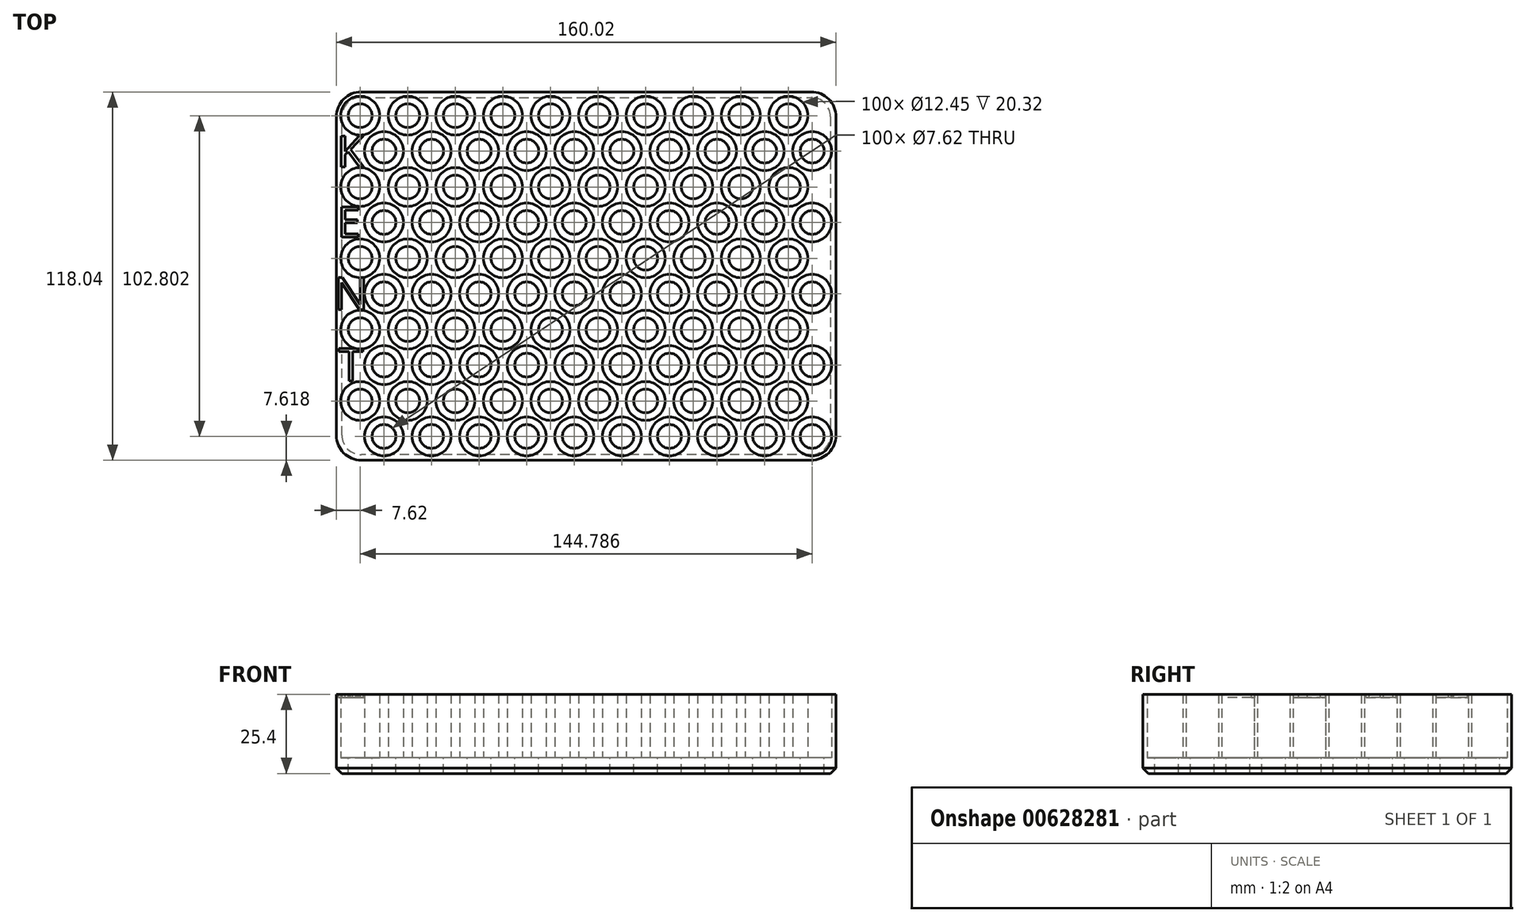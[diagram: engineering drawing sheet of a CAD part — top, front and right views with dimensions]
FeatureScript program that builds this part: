
annotation { "Feature Type Name" : "Feature", "Feature Type Description" : "" }
export const myFeature = defineFeature(function(context is Context, id is Id, definition is map)
    precondition{}
    {
        {
            var Q0;
            Q0=qCreatedBy(makeId("Top.planeOp"),FACE);
            var sketch = newSketch(context, id + "F0", { "sketchPlane" : qUnion([Q0])});
            skLineSegment(sketch, "E0.bottom", {"start": v(76.2, 76.2) * mm, "end": v(-76.2, 76.2) * mm});
            skLineSegment(sketch, "E0.right", {"start": v(-76.2, 76.2) * mm, "end": v(-76.2, -41.84) * mm});
            skPoint(sketch, "E0.middle", {"position": v(0, 0) * mm});
            skCircle(sketch, "E1", {"center": v(-68.58, 68.58) * mm, "radius": 6.22 * mm});
            skCircle(sketch, "E2", {"center": v(-68.58, 68.58) * mm, "radius": 3.81 * mm});
            skCircle(sketch, "E3.1.0.0", {"center": v(-53.34, 68.58) * mm, "radius": 3.81 * mm});
            skCircle(sketch, "E3.1.0.1", {"center": v(-53.34, 68.58) * mm, "radius": 6.22 * mm});
            skCircle(sketch, "E3.2.0.0", {"center": v(-38.1, 68.58) * mm, "radius": 3.81 * mm});
            skCircle(sketch, "E3.2.0.1", {"center": v(-38.1, 68.58) * mm, "radius": 6.22 * mm});
            skCircle(sketch, "E3.3.0.0", {"center": v(-22.86, 68.58) * mm, "radius": 3.81 * mm});
            skCircle(sketch, "E3.3.0.1", {"center": v(-22.86, 68.58) * mm, "radius": 6.22 * mm});
            skCircle(sketch, "E3.4.0.0", {"center": v(-7.62, 68.58) * mm, "radius": 3.81 * mm});
            skCircle(sketch, "E3.4.0.1", {"center": v(-7.62, 68.58) * mm, "radius": 6.22 * mm});
            skCircle(sketch, "E3.5.0.0", {"center": v(7.62, 68.58) * mm, "radius": 3.81 * mm});
            skCircle(sketch, "E3.5.0.1", {"center": v(7.62, 68.58) * mm, "radius": 6.22 * mm});
            skCircle(sketch, "E3.6.0.0", {"center": v(22.86, 68.58) * mm, "radius": 3.81 * mm});
            skCircle(sketch, "E3.6.0.1", {"center": v(22.86, 68.58) * mm, "radius": 6.22 * mm});
            skCircle(sketch, "E3.7.0.0", {"center": v(38.1, 68.58) * mm, "radius": 3.81 * mm});
            skCircle(sketch, "E3.7.0.1", {"center": v(38.1, 68.58) * mm, "radius": 6.22 * mm});
            skCircle(sketch, "E3.8.0.0", {"center": v(53.34, 68.58) * mm, "radius": 3.81 * mm});
            skCircle(sketch, "E3.8.0.1", {"center": v(53.34, 68.58) * mm, "radius": 6.22 * mm});
            skCircle(sketch, "E3.9.0.0", {"center": v(68.58, 68.58) * mm, "radius": 3.81 * mm});
            skCircle(sketch, "E3.9.0.1", {"center": v(68.58, 68.58) * mm, "radius": 6.22 * mm});
            skCircle(sketch, "E4.1.0.0", {"center": v(-68.58, 45.72) * mm, "radius": 3.81 * mm});
            skCircle(sketch, "E4.1.0.1", {"center": v(-68.58, 45.72) * mm, "radius": 6.22 * mm});
            skCircle(sketch, "E4.1.0.2", {"center": v(-22.86, 45.72) * mm, "radius": 3.81 * mm});
            skCircle(sketch, "E4.1.0.3", {"center": v(-53.34, 45.72) * mm, "radius": 3.81 * mm});
            skCircle(sketch, "E4.1.0.4", {"center": v(-38.1, 45.72) * mm, "radius": 3.81 * mm});
            skCircle(sketch, "E4.1.0.5", {"center": v(-38.1, 45.72) * mm, "radius": 6.22 * mm});
            skCircle(sketch, "E4.1.0.6", {"center": v(7.62, 45.72) * mm, "radius": 6.22 * mm});
            skCircle(sketch, "E4.1.0.7", {"center": v(22.86, 45.72) * mm, "radius": 3.81 * mm});
            skCircle(sketch, "E4.1.0.8", {"center": v(-22.86, 45.72) * mm, "radius": 6.22 * mm});
            skCircle(sketch, "E4.1.0.9", {"center": v(38.1, 45.72) * mm, "radius": 6.22 * mm});
            skCircle(sketch, "E4.1.0.10", {"center": v(-53.34, 45.72) * mm, "radius": 6.22 * mm});
            skCircle(sketch, "E4.1.0.11", {"center": v(-7.62, 45.72) * mm, "radius": 3.81 * mm});
            skCircle(sketch, "E4.1.0.12", {"center": v(22.86, 45.72) * mm, "radius": 6.22 * mm});
            skCircle(sketch, "E4.1.0.13", {"center": v(-7.62, 45.72) * mm, "radius": 6.22 * mm});
            skCircle(sketch, "E4.1.0.14", {"center": v(38.1, 45.72) * mm, "radius": 3.81 * mm});
            skCircle(sketch, "E4.1.0.15", {"center": v(7.62, 45.72) * mm, "radius": 3.81 * mm});
            skCircle(sketch, "E4.1.0.16", {"center": v(68.58, 45.72) * mm, "radius": 3.81 * mm});
            skCircle(sketch, "E4.1.0.17", {"center": v(53.34, 45.72) * mm, "radius": 3.81 * mm});
            skCircle(sketch, "E4.1.0.18", {"center": v(68.58, 45.72) * mm, "radius": 6.22 * mm});
            skCircle(sketch, "E4.1.0.19", {"center": v(53.34, 45.72) * mm, "radius": 6.22 * mm});
            skCircle(sketch, "E4.2.0.0", {"center": v(-68.58, 22.86) * mm, "radius": 3.81 * mm});
            skCircle(sketch, "E4.2.0.1", {"center": v(-68.58, 22.86) * mm, "radius": 6.22 * mm});
            skCircle(sketch, "E4.2.0.2", {"center": v(-22.86, 22.86) * mm, "radius": 3.81 * mm});
            skCircle(sketch, "E4.2.0.3", {"center": v(-53.34, 22.86) * mm, "radius": 3.81 * mm});
            skCircle(sketch, "E4.2.0.4", {"center": v(-38.1, 22.86) * mm, "radius": 3.81 * mm});
            skCircle(sketch, "E4.2.0.5", {"center": v(-38.1, 22.86) * mm, "radius": 6.22 * mm});
            skCircle(sketch, "E4.2.0.6", {"center": v(7.62, 22.86) * mm, "radius": 6.22 * mm});
            skCircle(sketch, "E4.2.0.7", {"center": v(22.86, 22.86) * mm, "radius": 3.81 * mm});
            skCircle(sketch, "E4.2.0.8", {"center": v(-22.86, 22.86) * mm, "radius": 6.22 * mm});
            skCircle(sketch, "E4.2.0.9", {"center": v(38.1, 22.86) * mm, "radius": 6.22 * mm});
            skCircle(sketch, "E4.2.0.10", {"center": v(-53.34, 22.86) * mm, "radius": 6.22 * mm});
            skCircle(sketch, "E4.2.0.11", {"center": v(-7.62, 22.86) * mm, "radius": 3.81 * mm});
            skCircle(sketch, "E4.2.0.12", {"center": v(22.86, 22.86) * mm, "radius": 6.22 * mm});
            skCircle(sketch, "E4.2.0.13", {"center": v(-7.62, 22.86) * mm, "radius": 6.22 * mm});
            skCircle(sketch, "E4.2.0.14", {"center": v(38.1, 22.86) * mm, "radius": 3.81 * mm});
            skCircle(sketch, "E4.2.0.15", {"center": v(7.62, 22.86) * mm, "radius": 3.81 * mm});
            skCircle(sketch, "E4.2.0.16", {"center": v(68.58, 22.86) * mm, "radius": 3.81 * mm});
            skCircle(sketch, "E4.2.0.17", {"center": v(53.34, 22.86) * mm, "radius": 3.81 * mm});
            skCircle(sketch, "E4.2.0.18", {"center": v(68.58, 22.86) * mm, "radius": 6.22 * mm});
            skCircle(sketch, "E4.2.0.19", {"center": v(53.34, 22.86) * mm, "radius": 6.22 * mm});
            skCircle(sketch, "E4.3.0.0", {"center": v(-68.58, 0) * mm, "radius": 3.81 * mm});
            skCircle(sketch, "E4.3.0.1", {"center": v(-68.58, 0) * mm, "radius": 6.22 * mm});
            skCircle(sketch, "E4.3.0.2", {"center": v(-22.86, 0) * mm, "radius": 3.81 * mm});
            skCircle(sketch, "E4.3.0.3", {"center": v(-53.34, 0) * mm, "radius": 3.81 * mm});
            skCircle(sketch, "E4.3.0.4", {"center": v(-38.1, 0) * mm, "radius": 3.81 * mm});
            skCircle(sketch, "E4.3.0.5", {"center": v(-38.1, 0) * mm, "radius": 6.22 * mm});
            skCircle(sketch, "E4.3.0.6", {"center": v(7.62, 0) * mm, "radius": 6.22 * mm});
            skCircle(sketch, "E4.3.0.7", {"center": v(22.86, 0) * mm, "radius": 3.81 * mm});
            skCircle(sketch, "E4.3.0.8", {"center": v(-22.86, 0) * mm, "radius": 6.22 * mm});
            skCircle(sketch, "E4.3.0.9", {"center": v(38.1, 0) * mm, "radius": 6.22 * mm});
            skCircle(sketch, "E4.3.0.10", {"center": v(-53.34, 0) * mm, "radius": 6.22 * mm});
            skCircle(sketch, "E4.3.0.11", {"center": v(-7.62, 0) * mm, "radius": 3.81 * mm});
            skCircle(sketch, "E4.3.0.12", {"center": v(22.86, 0) * mm, "radius": 6.22 * mm});
            skCircle(sketch, "E4.3.0.13", {"center": v(-7.62, 0) * mm, "radius": 6.22 * mm});
            skCircle(sketch, "E4.3.0.14", {"center": v(38.1, 0) * mm, "radius": 3.81 * mm});
            skCircle(sketch, "E4.3.0.15", {"center": v(7.62, 0) * mm, "radius": 3.81 * mm});
            skCircle(sketch, "E4.3.0.16", {"center": v(68.58, 0) * mm, "radius": 3.81 * mm});
            skCircle(sketch, "E4.3.0.17", {"center": v(53.34, 0) * mm, "radius": 3.81 * mm});
            skCircle(sketch, "E4.3.0.18", {"center": v(68.58, 0) * mm, "radius": 6.22 * mm});
            skCircle(sketch, "E4.3.0.19", {"center": v(53.34, 0) * mm, "radius": 6.22 * mm});
            skCircle(sketch, "E4.4.0.0", {"center": v(-68.58, -22.86) * mm, "radius": 3.81 * mm});
            skCircle(sketch, "E4.4.0.1", {"center": v(-68.58, -22.86) * mm, "radius": 6.22 * mm});
            skCircle(sketch, "E4.4.0.2", {"center": v(-22.86, -22.86) * mm, "radius": 3.81 * mm});
            skCircle(sketch, "E4.4.0.3", {"center": v(-53.34, -22.86) * mm, "radius": 3.81 * mm});
            skCircle(sketch, "E4.4.0.4", {"center": v(-38.1, -22.86) * mm, "radius": 3.81 * mm});
            skCircle(sketch, "E4.4.0.5", {"center": v(-38.1, -22.86) * mm, "radius": 6.22 * mm});
            skCircle(sketch, "E4.4.0.6", {"center": v(7.62, -22.86) * mm, "radius": 6.22 * mm});
            skCircle(sketch, "E4.4.0.7", {"center": v(22.86, -22.86) * mm, "radius": 3.81 * mm});
            skCircle(sketch, "E4.4.0.8", {"center": v(-22.86, -22.86) * mm, "radius": 6.22 * mm});
            skCircle(sketch, "E4.4.0.9", {"center": v(38.1, -22.86) * mm, "radius": 6.22 * mm});
            skCircle(sketch, "E4.4.0.10", {"center": v(-53.34, -22.86) * mm, "radius": 6.22 * mm});
            skCircle(sketch, "E4.4.0.11", {"center": v(-7.62, -22.86) * mm, "radius": 3.81 * mm});
            skCircle(sketch, "E4.4.0.12", {"center": v(22.86, -22.86) * mm, "radius": 6.22 * mm});
            skCircle(sketch, "E4.4.0.13", {"center": v(-7.62, -22.86) * mm, "radius": 6.22 * mm});
            skCircle(sketch, "E4.4.0.14", {"center": v(38.1, -22.86) * mm, "radius": 3.81 * mm});
            skCircle(sketch, "E4.4.0.15", {"center": v(7.62, -22.86) * mm, "radius": 3.81 * mm});
            skCircle(sketch, "E4.4.0.16", {"center": v(68.58, -22.86) * mm, "radius": 3.81 * mm});
            skCircle(sketch, "E4.4.0.17", {"center": v(53.34, -22.86) * mm, "radius": 3.81 * mm});
            skCircle(sketch, "E4.4.0.18", {"center": v(68.58, -22.86) * mm, "radius": 6.22 * mm});
            skCircle(sketch, "E4.4.0.19", {"center": v(53.34, -22.86) * mm, "radius": 6.22 * mm});
            skCircle(sketch, "E5", {"center": v(-60.95, 57.22) * mm, "radius": 6.22 * mm});
            skCircle(sketch, "E6", {"center": v(-60.95, 57.22) * mm, "radius": 3.81 * mm});
            skCircle(sketch, "E7.1.0.0", {"center": v(-60.96, 34.36) * mm, "radius": 3.81 * mm});
            skCircle(sketch, "E7.1.0.1", {"center": v(-60.96, 34.36) * mm, "radius": 6.22 * mm});
            skCircle(sketch, "E7.2.0.0", {"center": v(-60.97, 11.5) * mm, "radius": 3.81 * mm});
            skCircle(sketch, "E7.2.0.1", {"center": v(-60.97, 11.5) * mm, "radius": 6.22 * mm});
            skCircle(sketch, "E7.3.0.0", {"center": v(-60.97, -11.36) * mm, "radius": 3.81 * mm});
            skCircle(sketch, "E7.3.0.1", {"center": v(-60.97, -11.36) * mm, "radius": 6.22 * mm});
            skCircle(sketch, "E7.4.0.0", {"center": v(-60.98, -34.22) * mm, "radius": 3.81 * mm});
            skCircle(sketch, "E7.4.0.1", {"center": v(-60.98, -34.22) * mm, "radius": 6.22 * mm});
            skCircle(sketch, "E8.1.0.0", {"center": v(-45.71, 57.22) * mm, "radius": 3.81 * mm});
            skCircle(sketch, "E8.1.0.1", {"center": v(-45.71, 57.22) * mm, "radius": 6.22 * mm});
            skCircle(sketch, "E8.1.0.2", {"center": v(-45.72, 34.36) * mm, "radius": 3.81 * mm});
            skCircle(sketch, "E8.1.0.3", {"center": v(-45.72, 34.36) * mm, "radius": 6.22 * mm});
            skCircle(sketch, "E8.1.0.4", {"center": v(-45.73, 11.5) * mm, "radius": 3.81 * mm});
            skCircle(sketch, "E8.1.0.5", {"center": v(-45.73, 11.5) * mm, "radius": 6.22 * mm});
            skCircle(sketch, "E8.1.0.6", {"center": v(-45.73, -11.36) * mm, "radius": 3.81 * mm});
            skCircle(sketch, "E8.1.0.7", {"center": v(-45.73, -11.36) * mm, "radius": 6.22 * mm});
            skCircle(sketch, "E8.1.0.8", {"center": v(-45.74, -34.22) * mm, "radius": 3.81 * mm});
            skCircle(sketch, "E8.1.0.9", {"center": v(-45.74, -34.22) * mm, "radius": 6.22 * mm});
            skCircle(sketch, "E8.2.0.0", {"center": v(-30.47, 57.22) * mm, "radius": 3.81 * mm});
            skCircle(sketch, "E8.2.0.1", {"center": v(-30.47, 57.22) * mm, "radius": 6.22 * mm});
            skCircle(sketch, "E8.2.0.2", {"center": v(-30.48, 34.36) * mm, "radius": 3.81 * mm});
            skCircle(sketch, "E8.2.0.3", {"center": v(-30.48, 34.36) * mm, "radius": 6.22 * mm});
            skCircle(sketch, "E8.2.0.4", {"center": v(-30.49, 11.5) * mm, "radius": 3.81 * mm});
            skCircle(sketch, "E8.2.0.5", {"center": v(-30.49, 11.5) * mm, "radius": 6.22 * mm});
            skCircle(sketch, "E8.2.0.6", {"center": v(-30.5, -11.36) * mm, "radius": 3.81 * mm});
            skCircle(sketch, "E8.2.0.7", {"center": v(-30.5, -11.36) * mm, "radius": 6.22 * mm});
            skCircle(sketch, "E8.2.0.8", {"center": v(-30.5, -34.22) * mm, "radius": 3.81 * mm});
            skCircle(sketch, "E8.2.0.9", {"center": v(-30.5, -34.22) * mm, "radius": 6.22 * mm});
            skCircle(sketch, "E8.3.0.0", {"center": v(-15.23, 57.22) * mm, "radius": 3.81 * mm});
            skCircle(sketch, "E8.3.0.1", {"center": v(-15.23, 57.22) * mm, "radius": 6.22 * mm});
            skCircle(sketch, "E8.3.0.2", {"center": v(-15.24, 34.36) * mm, "radius": 3.81 * mm});
            skCircle(sketch, "E8.3.0.3", {"center": v(-15.24, 34.36) * mm, "radius": 6.22 * mm});
            skCircle(sketch, "E8.3.0.4", {"center": v(-15.25, 11.5) * mm, "radius": 3.81 * mm});
            skCircle(sketch, "E8.3.0.5", {"center": v(-15.25, 11.5) * mm, "radius": 6.22 * mm});
            skCircle(sketch, "E8.3.0.6", {"center": v(-15.25, -11.36) * mm, "radius": 3.81 * mm});
            skCircle(sketch, "E8.3.0.7", {"center": v(-15.25, -11.36) * mm, "radius": 6.22 * mm});
            skCircle(sketch, "E8.3.0.8", {"center": v(-15.26, -34.22) * mm, "radius": 3.81 * mm});
            skCircle(sketch, "E8.3.0.9", {"center": v(-15.26, -34.22) * mm, "radius": 6.22 * mm});
            skCircle(sketch, "E8.4.0.0", {"center": v(0, 57.22) * mm, "radius": 3.81 * mm});
            skCircle(sketch, "E8.4.0.1", {"center": v(0, 57.22) * mm, "radius": 6.22 * mm});
            skCircle(sketch, "E8.4.0.2", {"center": v(0, 34.36) * mm, "radius": 3.81 * mm});
            skCircle(sketch, "E8.4.0.3", {"center": v(0, 34.36) * mm, "radius": 6.22 * mm});
            skCircle(sketch, "E8.4.0.4", {"center": v(0, 11.5) * mm, "radius": 3.81 * mm});
            skCircle(sketch, "E8.4.0.5", {"center": v(0, 11.5) * mm, "radius": 6.22 * mm});
            skCircle(sketch, "E8.4.0.6", {"center": v(-0.01, -11.36) * mm, "radius": 3.81 * mm});
            skCircle(sketch, "E8.4.0.7", {"center": v(-0.01, -11.36) * mm, "radius": 6.22 * mm});
            skCircle(sketch, "E8.4.0.8", {"center": v(-0.02, -34.22) * mm, "radius": 3.81 * mm});
            skCircle(sketch, "E8.4.0.9", {"center": v(-0.02, -34.22) * mm, "radius": 6.22 * mm});
            skCircle(sketch, "E8.5.0.0", {"center": v(15.25, 57.22) * mm, "radius": 3.81 * mm});
            skCircle(sketch, "E8.5.0.1", {"center": v(15.25, 57.22) * mm, "radius": 6.22 * mm});
            skCircle(sketch, "E8.5.0.2", {"center": v(15.24, 34.36) * mm, "radius": 3.81 * mm});
            skCircle(sketch, "E8.5.0.3", {"center": v(15.24, 34.36) * mm, "radius": 6.22 * mm});
            skCircle(sketch, "E8.5.0.4", {"center": v(15.23, 11.5) * mm, "radius": 3.81 * mm});
            skCircle(sketch, "E8.5.0.5", {"center": v(15.23, 11.5) * mm, "radius": 6.22 * mm});
            skCircle(sketch, "E8.5.0.6", {"center": v(15.23, -11.36) * mm, "radius": 3.81 * mm});
            skCircle(sketch, "E8.5.0.7", {"center": v(15.23, -11.36) * mm, "radius": 6.22 * mm});
            skCircle(sketch, "E8.5.0.8", {"center": v(15.22, -34.22) * mm, "radius": 3.81 * mm});
            skCircle(sketch, "E8.5.0.9", {"center": v(15.22, -34.22) * mm, "radius": 6.22 * mm});
            skCircle(sketch, "E8.6.0.0", {"center": v(30.49, 57.22) * mm, "radius": 3.81 * mm});
            skCircle(sketch, "E8.6.0.1", {"center": v(30.49, 57.22) * mm, "radius": 6.22 * mm});
            skCircle(sketch, "E8.6.0.2", {"center": v(30.48, 34.36) * mm, "radius": 3.81 * mm});
            skCircle(sketch, "E8.6.0.3", {"center": v(30.48, 34.36) * mm, "radius": 6.22 * mm});
            skCircle(sketch, "E8.6.0.4", {"center": v(30.47, 11.5) * mm, "radius": 3.81 * mm});
            skCircle(sketch, "E8.6.0.5", {"center": v(30.47, 11.5) * mm, "radius": 6.22 * mm});
            skCircle(sketch, "E8.6.0.6", {"center": v(30.47, -11.36) * mm, "radius": 3.81 * mm});
            skCircle(sketch, "E8.6.0.7", {"center": v(30.47, -11.36) * mm, "radius": 6.22 * mm});
            skCircle(sketch, "E8.6.0.8", {"center": v(30.46, -34.22) * mm, "radius": 3.81 * mm});
            skCircle(sketch, "E8.6.0.9", {"center": v(30.46, -34.22) * mm, "radius": 6.22 * mm});
            skCircle(sketch, "E8.7.0.0", {"center": v(45.73, 57.22) * mm, "radius": 3.81 * mm});
            skCircle(sketch, "E8.7.0.1", {"center": v(45.73, 57.22) * mm, "radius": 6.22 * mm});
            skCircle(sketch, "E8.7.0.2", {"center": v(45.72, 34.36) * mm, "radius": 3.81 * mm});
            skCircle(sketch, "E8.7.0.3", {"center": v(45.72, 34.36) * mm, "radius": 6.22 * mm});
            skCircle(sketch, "E8.7.0.4", {"center": v(45.71, 11.5) * mm, "radius": 3.81 * mm});
            skCircle(sketch, "E8.7.0.5", {"center": v(45.71, 11.5) * mm, "radius": 6.22 * mm});
            skCircle(sketch, "E8.7.0.6", {"center": v(45.7, -11.36) * mm, "radius": 3.81 * mm});
            skCircle(sketch, "E8.7.0.7", {"center": v(45.7, -11.36) * mm, "radius": 6.22 * mm});
            skCircle(sketch, "E8.7.0.8", {"center": v(45.7, -34.22) * mm, "radius": 3.81 * mm});
            skCircle(sketch, "E8.7.0.9", {"center": v(45.7, -34.22) * mm, "radius": 6.22 * mm});
            skCircle(sketch, "E8.8.0.0", {"center": v(60.97, 57.22) * mm, "radius": 3.81 * mm});
            skCircle(sketch, "E8.8.0.1", {"center": v(60.97, 57.22) * mm, "radius": 6.22 * mm});
            skCircle(sketch, "E8.8.0.2", {"center": v(60.96, 34.36) * mm, "radius": 3.81 * mm});
            skCircle(sketch, "E8.8.0.3", {"center": v(60.96, 34.36) * mm, "radius": 6.22 * mm});
            skCircle(sketch, "E8.8.0.4", {"center": v(60.95, 11.5) * mm, "radius": 3.81 * mm});
            skCircle(sketch, "E8.8.0.5", {"center": v(60.95, 11.5) * mm, "radius": 6.22 * mm});
            skCircle(sketch, "E8.8.0.6", {"center": v(60.95, -11.36) * mm, "radius": 3.81 * mm});
            skCircle(sketch, "E8.8.0.7", {"center": v(60.95, -11.36) * mm, "radius": 6.22 * mm});
            skCircle(sketch, "E8.8.0.8", {"center": v(60.94, -34.22) * mm, "radius": 3.81 * mm});
            skCircle(sketch, "E8.8.0.9", {"center": v(60.94, -34.22) * mm, "radius": 6.22 * mm});
            skCircle(sketch, "E8.9.0.0", {"center": v(76.2, 57.22) * mm, "radius": 3.81 * mm});
            skCircle(sketch, "E8.9.0.1", {"center": v(76.2, 57.22) * mm, "radius": 6.22 * mm});
            skCircle(sketch, "E8.9.0.2", {"center": v(76.2, 34.36) * mm, "radius": 3.81 * mm});
            skCircle(sketch, "E8.9.0.3", {"center": v(76.2, 34.36) * mm, "radius": 6.22 * mm});
            skCircle(sketch, "E8.9.0.4", {"center": v(76.2, 11.5) * mm, "radius": 3.81 * mm});
            skCircle(sketch, "E8.9.0.5", {"center": v(76.2, 11.5) * mm, "radius": 6.22 * mm});
            skCircle(sketch, "E8.9.0.6", {"center": v(76.19, -11.36) * mm, "radius": 3.81 * mm});
            skCircle(sketch, "E8.9.0.7", {"center": v(76.19, -11.36) * mm, "radius": 6.22 * mm});
            skCircle(sketch, "E8.9.0.8", {"center": v(76.18, -34.22) * mm, "radius": 3.81 * mm});
            skCircle(sketch, "E8.9.0.9", {"center": v(76.18, -34.22) * mm, "radius": 6.22 * mm});
            skLineSegment(sketch, "E9", {"start": v(76.2, 76.2) * mm, "end": v(83.82, 76.2) * mm});
            skLineSegment(sketch, "E10", {"start": v(83.82, 76.2) * mm, "end": v(83.82, -41.84) * mm});
            skLineSegment(sketch, "E11", {"start": v(60.94, -41.84) * mm, "end": v(-60.98, -41.84) * mm});
            skLineSegment(sketch, "E12", {"start": v(-44.38, -41.84) * mm, "end": v(-76.2, -41.84) * mm});
            skLineSegment(sketch, "E13", {"start": v(51.23, -41.84) * mm, "end": v(83.82, -41.84) * mm});
            skPoint(sketch, "E14.end.orphan", {"position": v(76.2, -76.2) * mm});
            skPoint(sketch, "E15.orphan", {"position": v(-76.2, -76.2) * mm});
            skSolve(sketch);
        }
        {
            var Q0;
            Q0=makeQuery(id+"F0.imprint","IMPRINT",FACE,{"disambiguationData":[TD([[makeQuery(id+"F0.imprint","IMPRINT",EDGE,{"derivedFrom":sQuery(id+"F0.wireOp",EDGE,"E8.2.0.6")}),-1.0]])]});
            var Q1;
            Q1=makeQuery(id+"F0.imprint","IMPRINT",FACE,{"disambiguationData":[TD([[makeQuery(id+"F0.imprint","IMPRINT",EDGE,{"derivedFrom":sQuery(id+"F0.wireOp",EDGE,"E4.3.0.4")}),-1.0]])]});
            var Q2;
            Q2=makeQuery(id+"F0.imprint","IMPRINT",FACE,{"disambiguationData":[TD([[makeQuery(id+"F0.imprint","IMPRINT",EDGE,{"derivedFrom":sQuery(id+"F0.wireOp",EDGE,"E8.1.0.6")}),-1.0]])]});
            var Q3;
            Q3=makeQuery(id+"F0.imprint","IMPRINT",FACE,{"disambiguationData":[TD([[makeQuery(id+"F0.imprint","IMPRINT",EDGE,{"derivedFrom":sQuery(id+"F0.wireOp",EDGE,"E4.4.0.4")}),-1.0]])]});
            var Q4;
            Q4=makeQuery(id+"F0.imprint","IMPRINT",FACE,{"disambiguationData":[TD([[makeQuery(id+"F0.imprint","IMPRINT",EDGE,{"derivedFrom":sQuery(id+"F0.wireOp",EDGE,"E8.1.0.8")}),-1.0]])]});
            var Q5;
            Q5=makeQuery(id+"F0.imprint","IMPRINT",FACE,{"disambiguationData":[TD([[makeQuery(id+"F0.imprint","IMPRINT",EDGE,{"derivedFrom":sQuery(id+"F0.wireOp",EDGE,"E8.2.0.8")}),-1.0]])]});
            var Q6;
            Q6=makeQuery(id+"F0.imprint","IMPRINT",FACE,{"disambiguationData":[TD([[makeQuery(id+"F0.imprint","IMPRINT",EDGE,{"derivedFrom":sQuery(id+"F0.wireOp",EDGE,"E4.4.0.2")}),-1.0]])]});
            var Q7;
            Q7=makeQuery(id+"F0.imprint","IMPRINT",FACE,{"disambiguationData":[TD([[makeQuery(id+"F0.imprint","IMPRINT",EDGE,{"derivedFrom":sQuery(id+"F0.wireOp",EDGE,"E8.3.0.6")}),-1.0]])]});
            var Q8;
            Q8=makeQuery(id+"F0.imprint","IMPRINT",FACE,{"disambiguationData":[TD([[makeQuery(id+"F0.imprint","IMPRINT",EDGE,{"derivedFrom":sQuery(id+"F0.wireOp",EDGE,"E4.3.0.2")}),-1.0]])]});
            var Q9;
            Q9=makeQuery(id+"F0.imprint","IMPRINT",FACE,{"disambiguationData":[TD([[makeQuery(id+"F0.imprint","IMPRINT",EDGE,{"derivedFrom":sQuery(id+"F0.wireOp",EDGE,"E4.3.0.3")}),-1.0]])]});
            var Q10;
            Q10=makeQuery(id+"F0.imprint","IMPRINT",FACE,{"disambiguationData":[TD([[makeQuery(id+"F0.imprint","IMPRINT",EDGE,{"derivedFrom":sQuery(id+"F0.wireOp",EDGE,"E7.3.0.0")}),-1.0]])]});
            var Q11;
            Q11=makeQuery(id+"F0.imprint","IMPRINT",FACE,{"disambiguationData":[TD([[makeQuery(id+"F0.imprint","IMPRINT",EDGE,{"derivedFrom":sQuery(id+"F0.wireOp",EDGE,"E4.4.0.3")}),-1.0]])]});
            var Q12;
            Q12=makeQuery(id+"F0.imprint","IMPRINT",FACE,{"disambiguationData":[TD([[makeQuery(id+"F0.imprint","IMPRINT",EDGE,{"derivedFrom":sQuery(id+"F0.wireOp",EDGE,"E7.4.0.0")}),-1.0]])]});
            var Q13;
            Q13=makeQuery(id+"F0.imprint","IMPRINT",FACE,{"disambiguationData":[TD([[makeQuery(id+"F0.imprint","IMPRINT",EDGE,{"derivedFrom":sQuery(id+"F0.wireOp",EDGE,"E4.4.0.0")}),-1.0]])]});
            var Q14;
            Q14=makeQuery(id+"F0.imprint","IMPRINT",FACE,{"disambiguationData":[TD([[makeQuery(id+"F0.imprint","IMPRINT",EDGE,{"derivedFrom":sQuery(id+"F0.wireOp",EDGE,"E4.3.0.0")}),-1.0]])]});
            var Q15;
            Q15=makeQuery(id+"F0.imprint","IMPRINT",FACE,{"disambiguationData":[TD([[makeQuery(id+"F0.imprint","IMPRINT",EDGE,{"derivedFrom":sQuery(id+"F0.wireOp",EDGE,"E4.3.0.11")}),-1.0]])]});
            var Q16;
            Q16=makeQuery(id+"F0.imprint","IMPRINT",FACE,{"disambiguationData":[TD([[makeQuery(id+"F0.imprint","IMPRINT",EDGE,{"derivedFrom":sQuery(id+"F0.wireOp",EDGE,"E8.4.0.6")}),-1.0]])]});
            var Q17;
            Q17=makeQuery(id+"F0.imprint","IMPRINT",FACE,{"disambiguationData":[TD([[makeQuery(id+"F0.imprint","IMPRINT",EDGE,{"derivedFrom":sQuery(id+"F0.wireOp",EDGE,"E4.4.0.11")}),-1.0]])]});
            var Q18;
            Q18=makeQuery(id+"F0.imprint","IMPRINT",FACE,{"disambiguationData":[TD([[makeQuery(id+"F0.imprint","IMPRINT",EDGE,{"derivedFrom":sQuery(id+"F0.wireOp",EDGE,"E8.3.0.8")}),-1.0]])]});
            var Q19;
            Q19=makeQuery(id+"F0.imprint","IMPRINT",FACE,{"disambiguationData":[TD([[makeQuery(id+"F0.imprint","IMPRINT",EDGE,{"derivedFrom":sQuery(id+"F0.wireOp",EDGE,"E8.4.0.8")}),-1.0]])]});
            var Q20;
            Q20=makeQuery(id+"F0.imprint","IMPRINT",FACE,{"disambiguationData":[TD([[makeQuery(id+"F0.imprint","IMPRINT",EDGE,{"derivedFrom":sQuery(id+"F0.wireOp",EDGE,"E4.4.0.6")}),1.0]])]});
            var Q21;
            Q21=makeQuery(id+"F0.imprint","IMPRINT",FACE,{"disambiguationData":[TD([[makeQuery(id+"F0.imprint","IMPRINT",EDGE,{"derivedFrom":sQuery(id+"F0.wireOp",EDGE,"E8.5.0.8")}),-1.0]])]});
            var Q22;
            Q22=makeQuery(id+"F0.imprint","IMPRINT",FACE,{"disambiguationData":[TD([[makeQuery(id+"F0.imprint","IMPRINT",EDGE,{"derivedFrom":sQuery(id+"F0.wireOp",EDGE,"E4.4.0.7")}),-1.0]])]});
            var Q23;
            Q23=makeQuery(id+"F0.imprint","IMPRINT",FACE,{"disambiguationData":[TD([[makeQuery(id+"F0.imprint","IMPRINT",EDGE,{"derivedFrom":sQuery(id+"F0.wireOp",EDGE,"E8.5.0.6")}),-1.0]])]});
            var Q24;
            Q24=makeQuery(id+"F0.imprint","IMPRINT",FACE,{"disambiguationData":[TD([[makeQuery(id+"F0.imprint","IMPRINT",EDGE,{"derivedFrom":sQuery(id+"F0.wireOp",EDGE,"E4.3.0.6")}),1.0]])]});
            var Q25;
            Q25=makeQuery(id+"F0.imprint","IMPRINT",FACE,{"disambiguationData":[TD([[makeQuery(id+"F0.imprint","IMPRINT",EDGE,{"derivedFrom":sQuery(id+"F0.wireOp",EDGE,"E8.3.0.4")}),-1.0]])]});
            var Q26;
            Q26=makeQuery(id+"F0.imprint","IMPRINT",FACE,{"disambiguationData":[TD([[makeQuery(id+"F0.imprint","IMPRINT",EDGE,{"derivedFrom":sQuery(id+"F0.wireOp",EDGE,"E8.2.0.4")}),-1.0]])]});
            var Q27;
            Q27=makeQuery(id+"F0.imprint","IMPRINT",FACE,{"disambiguationData":[TD([[makeQuery(id+"F0.imprint","IMPRINT",EDGE,{"derivedFrom":sQuery(id+"F0.wireOp",EDGE,"E8.1.0.4")}),-1.0]])]});
            var Q28;
            Q28=makeQuery(id+"F0.imprint","IMPRINT",FACE,{"disambiguationData":[TD([[makeQuery(id+"F0.imprint","IMPRINT",EDGE,{"derivedFrom":sQuery(id+"F0.wireOp",EDGE,"E7.2.0.0")}),-1.0]])]});
            var Q29;
            Q29=makeQuery(id+"F0.imprint","IMPRINT",FACE,{"disambiguationData":[TD([[makeQuery(id+"F0.imprint","IMPRINT",EDGE,{"derivedFrom":sQuery(id+"F0.wireOp",EDGE,"E4.2.0.3")}),-1.0]])]});
            var Q30;
            Q30=makeQuery(id+"F0.imprint","IMPRINT",FACE,{"disambiguationData":[TD([[makeQuery(id+"F0.imprint","IMPRINT",EDGE,{"derivedFrom":sQuery(id+"F0.wireOp",EDGE,"E4.2.0.4")}),-1.0]])]});
            var Q31;
            Q31=makeQuery(id+"F0.imprint","IMPRINT",FACE,{"disambiguationData":[TD([[makeQuery(id+"F0.imprint","IMPRINT",EDGE,{"derivedFrom":sQuery(id+"F0.wireOp",EDGE,"E4.2.0.2")}),-1.0]])]});
            var Q32;
            Q32=makeQuery(id+"F0.imprint","IMPRINT",FACE,{"disambiguationData":[TD([[makeQuery(id+"F0.imprint","IMPRINT",EDGE,{"derivedFrom":sQuery(id+"F0.wireOp",EDGE,"E4.2.0.11")}),-1.0]])]});
            var Q33;
            Q33=makeQuery(id+"F0.imprint","IMPRINT",FACE,{"disambiguationData":[TD([[makeQuery(id+"F0.imprint","IMPRINT",EDGE,{"derivedFrom":sQuery(id+"F0.wireOp",EDGE,"E8.4.0.4")}),-1.0]])]});
            var Q34;
            Q34=makeQuery(id+"F0.imprint","IMPRINT",FACE,{"disambiguationData":[TD([[makeQuery(id+"F0.imprint","IMPRINT",EDGE,{"derivedFrom":sQuery(id+"F0.wireOp",EDGE,"E8.5.0.4")}),-1.0]])]});
            var Q35;
            Q35=makeQuery(id+"F0.imprint","IMPRINT",FACE,{"disambiguationData":[TD([[makeQuery(id+"F0.imprint","IMPRINT",EDGE,{"derivedFrom":sQuery(id+"F0.wireOp",EDGE,"E8.9.0.8")}),-1.0]])]});
            var Q36;
            Q36=makeQuery(id+"F0.imprint","IMPRINT",FACE,{"disambiguationData":[TD([[makeQuery(id+"F0.imprint","IMPRINT",EDGE,{"derivedFrom":sQuery(id+"F0.wireOp",EDGE,"E8.8.0.8")}),-1.0]])]});
            var Q37;
            Q37=makeQuery(id+"F0.imprint","IMPRINT",FACE,{"disambiguationData":[TD([[makeQuery(id+"F0.imprint","IMPRINT",EDGE,{"derivedFrom":sQuery(id+"F0.wireOp",EDGE,"E8.7.0.8")}),-1.0]])]});
            var Q38;
            Q38=makeQuery(id+"F0.imprint","IMPRINT",FACE,{"disambiguationData":[TD([[makeQuery(id+"F0.imprint","IMPRINT",EDGE,{"derivedFrom":sQuery(id+"F0.wireOp",EDGE,"E8.6.0.8")}),-1.0]])]});
            var Q39;
            Q39=makeQuery(id+"F0.imprint","IMPRINT",FACE,{"disambiguationData":[TD([[makeQuery(id+"F0.imprint","IMPRINT",EDGE,{"derivedFrom":sQuery(id+"F0.wireOp",EDGE,"E4.4.0.9")}),1.0]])]});
            var Q40;
            Q40=makeQuery(id+"F0.imprint","IMPRINT",FACE,{"disambiguationData":[TD([[makeQuery(id+"F0.imprint","IMPRINT",EDGE,{"derivedFrom":sQuery(id+"F0.wireOp",EDGE,"E4.4.0.17")}),-1.0]])]});
            var Q41;
            Q41=makeQuery(id+"F0.imprint","IMPRINT",FACE,{"disambiguationData":[TD([[makeQuery(id+"F0.imprint","IMPRINT",EDGE,{"derivedFrom":sQuery(id+"F0.wireOp",EDGE,"E4.4.0.16")}),-1.0]])]});
            var Q42;
            Q42=makeQuery(id+"F0.imprint","IMPRINT",FACE,{"disambiguationData":[TD([[makeQuery(id+"F0.imprint","IMPRINT",EDGE,{"derivedFrom":sQuery(id+"F0.wireOp",EDGE,"E8.8.0.6")}),-1.0]])]});
            var Q43;
            Q43=makeQuery(id+"F0.imprint","IMPRINT",FACE,{"disambiguationData":[TD([[makeQuery(id+"F0.imprint","IMPRINT",EDGE,{"derivedFrom":sQuery(id+"F0.wireOp",EDGE,"E8.9.0.6")}),-1.0]])]});
            var Q44;
            Q44=makeQuery(id+"F0.imprint","IMPRINT",FACE,{"disambiguationData":[TD([[makeQuery(id+"F0.imprint","IMPRINT",EDGE,{"derivedFrom":sQuery(id+"F0.wireOp",EDGE,"E8.7.0.6")}),-1.0]])]});
            var Q45;
            Q45=makeQuery(id+"F0.imprint","IMPRINT",FACE,{"disambiguationData":[TD([[makeQuery(id+"F0.imprint","IMPRINT",EDGE,{"derivedFrom":sQuery(id+"F0.wireOp",EDGE,"E8.6.0.6")}),-1.0]])]});
            var Q46;
            Q46=makeQuery(id+"F0.imprint","IMPRINT",FACE,{"disambiguationData":[TD([[makeQuery(id+"F0.imprint","IMPRINT",EDGE,{"derivedFrom":sQuery(id+"F0.wireOp",EDGE,"E4.3.0.9")}),1.0]])]});
            var Q47;
            Q47=makeQuery(id+"F0.imprint","IMPRINT",FACE,{"disambiguationData":[TD([[makeQuery(id+"F0.imprint","IMPRINT",EDGE,{"derivedFrom":sQuery(id+"F0.wireOp",EDGE,"E4.3.0.7")}),-1.0]])]});
            var Q48;
            Q48=makeQuery(id+"F0.imprint","IMPRINT",FACE,{"disambiguationData":[TD([[makeQuery(id+"F0.imprint","IMPRINT",EDGE,{"derivedFrom":sQuery(id+"F0.wireOp",EDGE,"E4.3.0.17")}),-1.0]])]});
            var Q49;
            Q49=makeQuery(id+"F0.imprint","IMPRINT",FACE,{"disambiguationData":[TD([[makeQuery(id+"F0.imprint","IMPRINT",EDGE,{"derivedFrom":sQuery(id+"F0.wireOp",EDGE,"E4.3.0.16")}),-1.0]])]});
            var Q50;
            Q50=makeQuery(id+"F0.imprint","IMPRINT",FACE,{"disambiguationData":[TD([[makeQuery(id+"F0.imprint","IMPRINT",EDGE,{"derivedFrom":sQuery(id+"F0.wireOp",EDGE,"E8.9.0.4")}),-1.0]])]});
            var Q51;
            Q51=makeQuery(id+"F0.imprint","IMPRINT",FACE,{"disambiguationData":[TD([[makeQuery(id+"F0.imprint","IMPRINT",EDGE,{"derivedFrom":sQuery(id+"F0.wireOp",EDGE,"E8.8.0.4")}),-1.0]])]});
            var Q52;
            Q52=makeQuery(id+"F0.imprint","IMPRINT",FACE,{"disambiguationData":[TD([[makeQuery(id+"F0.imprint","IMPRINT",EDGE,{"derivedFrom":sQuery(id+"F0.wireOp",EDGE,"E8.7.0.4")}),-1.0]])]});
            var Q53;
            Q53=makeQuery(id+"F0.imprint","IMPRINT",FACE,{"disambiguationData":[TD([[makeQuery(id+"F0.imprint","IMPRINT",EDGE,{"derivedFrom":sQuery(id+"F0.wireOp",EDGE,"E8.6.0.4")}),-1.0]])]});
            var Q54;
            Q54=makeQuery(id+"F0.imprint","IMPRINT",FACE,{"disambiguationData":[TD([[makeQuery(id+"F0.imprint","IMPRINT",EDGE,{"derivedFrom":sQuery(id+"F0.wireOp",EDGE,"E4.2.0.7")}),-1.0]])]});
            var Q55;
            Q55=makeQuery(id+"F0.imprint","IMPRINT",FACE,{"disambiguationData":[TD([[makeQuery(id+"F0.imprint","IMPRINT",EDGE,{"derivedFrom":sQuery(id+"F0.wireOp",EDGE,"E4.2.0.9")}),1.0]])]});
            var Q56;
            Q56=makeQuery(id+"F0.imprint","IMPRINT",FACE,{"disambiguationData":[TD([[makeQuery(id+"F0.imprint","IMPRINT",EDGE,{"derivedFrom":sQuery(id+"F0.wireOp",EDGE,"E4.2.0.6")}),1.0]])]});
            var Q57;
            Q57=makeQuery(id+"F0.imprint","IMPRINT",FACE,{"disambiguationData":[TD([[makeQuery(id+"F0.imprint","IMPRINT",EDGE,{"derivedFrom":sQuery(id+"F0.wireOp",EDGE,"E8.5.0.2")}),-1.0]])]});
            var Q58;
            Q58=makeQuery(id+"F0.imprint","IMPRINT",FACE,{"disambiguationData":[TD([[makeQuery(id+"F0.imprint","IMPRINT",EDGE,{"derivedFrom":sQuery(id+"F0.wireOp",EDGE,"E8.6.0.2")}),-1.0]])]});
            var Q59;
            Q59=makeQuery(id+"F0.imprint","IMPRINT",FACE,{"disambiguationData":[TD([[makeQuery(id+"F0.imprint","IMPRINT",EDGE,{"derivedFrom":sQuery(id+"F0.wireOp",EDGE,"E8.4.0.2")}),-1.0]])]});
            var Q60;
            Q60=makeQuery(id+"F0.imprint","IMPRINT",FACE,{"disambiguationData":[TD([[makeQuery(id+"F0.imprint","IMPRINT",EDGE,{"derivedFrom":sQuery(id+"F0.wireOp",EDGE,"E8.3.0.2")}),-1.0]])]});
            var Q61;
            Q61=makeQuery(id+"F0.imprint","IMPRINT",FACE,{"disambiguationData":[TD([[makeQuery(id+"F0.imprint","IMPRINT",EDGE,{"derivedFrom":sQuery(id+"F0.wireOp",EDGE,"E8.1.0.0")}),-1.0]])]});
            var Q62;
            Q62=makeQuery(id+"F0.imprint","IMPRINT",FACE,{"disambiguationData":[TD([[makeQuery(id+"F0.imprint","IMPRINT",EDGE,{"derivedFrom":sQuery(id+"F0.wireOp",EDGE,"E5")}),1.0]])]});
            var Q63;
            Q63=makeQuery(id+"F0.imprint","IMPRINT",FACE,{"disambiguationData":[TD([[makeQuery(id+"F0.imprint","IMPRINT",EDGE,{"derivedFrom":sQuery(id+"F0.wireOp",EDGE,"E4.1.0.0")}),-1.0]])]});
            var Q64;
            Q64=makeQuery(id+"F0.imprint","IMPRINT",FACE,{"disambiguationData":[TD([[makeQuery(id+"F0.imprint","IMPRINT",EDGE,{"derivedFrom":sQuery(id+"F0.wireOp",EDGE,"E4.1.0.3")}),-1.0]])]});
            var Q65;
            Q65=makeQuery(id+"F0.imprint","IMPRINT",FACE,{"disambiguationData":[TD([[makeQuery(id+"F0.imprint","IMPRINT",EDGE,{"derivedFrom":sQuery(id+"F0.wireOp",EDGE,"E4.2.0.0")}),-1.0]])]});
            var Q66;
            Q66=makeQuery(id+"F0.imprint","IMPRINT",FACE,{"disambiguationData":[TD([[makeQuery(id+"F0.imprint","IMPRINT",EDGE,{"derivedFrom":sQuery(id+"F0.wireOp",EDGE,"E7.1.0.0")}),-1.0]])]});
            var Q67;
            Q67=makeQuery(id+"F0.imprint","IMPRINT",FACE,{"disambiguationData":[TD([[makeQuery(id+"F0.imprint","IMPRINT",EDGE,{"derivedFrom":sQuery(id+"F0.wireOp",EDGE,"E8.1.0.2")}),-1.0]])]});
            var Q68;
            Q68=makeQuery(id+"F0.imprint","IMPRINT",FACE,{"disambiguationData":[TD([[makeQuery(id+"F0.imprint","IMPRINT",EDGE,{"derivedFrom":sQuery(id+"F0.wireOp",EDGE,"E8.2.0.2")}),-1.0]])]});
            var Q69;
            Q69=makeQuery(id+"F0.imprint","IMPRINT",FACE,{"disambiguationData":[TD([[makeQuery(id+"F0.imprint","IMPRINT",EDGE,{"derivedFrom":sQuery(id+"F0.wireOp",EDGE,"E4.1.0.4")}),-1.0]])]});
            var Q70;
            Q70=makeQuery(id+"F0.imprint","IMPRINT",FACE,{"disambiguationData":[TD([[makeQuery(id+"F0.imprint","IMPRINT",EDGE,{"derivedFrom":sQuery(id+"F0.wireOp",EDGE,"E4.1.0.2")}),-1.0]])]});
            var Q71;
            Q71=makeQuery(id+"F0.imprint","IMPRINT",FACE,{"disambiguationData":[TD([[makeQuery(id+"F0.imprint","IMPRINT",EDGE,{"derivedFrom":sQuery(id+"F0.wireOp",EDGE,"E8.2.0.0")}),-1.0]])]});
            var Q72;
            Q72=makeQuery(id+"F0.imprint","IMPRINT",FACE,{"disambiguationData":[TD([[makeQuery(id+"F0.imprint","IMPRINT",EDGE,{"derivedFrom":sQuery(id+"F0.wireOp",EDGE,"E8.3.0.0")}),-1.0]])]});
            var Q73;
            Q73=makeQuery(id+"F0.imprint","IMPRINT",FACE,{"disambiguationData":[TD([[makeQuery(id+"F0.imprint","IMPRINT",EDGE,{"derivedFrom":sQuery(id+"F0.wireOp",EDGE,"E8.4.0.0")}),-1.0]])]});
            var Q74;
            Q74=makeQuery(id+"F0.imprint","IMPRINT",FACE,{"disambiguationData":[TD([[makeQuery(id+"F0.imprint","IMPRINT",EDGE,{"derivedFrom":sQuery(id+"F0.wireOp",EDGE,"E4.1.0.11")}),-1.0]])]});
            var Q75;
            Q75=makeQuery(id+"F0.imprint","IMPRINT",FACE,{"disambiguationData":[TD([[makeQuery(id+"F0.imprint","IMPRINT",EDGE,{"derivedFrom":sQuery(id+"F0.wireOp",EDGE,"E4.1.0.6")}),1.0]])]});
            var Q76;
            Q76=makeQuery(id+"F0.imprint","IMPRINT",FACE,{"disambiguationData":[TD([[makeQuery(id+"F0.imprint","IMPRINT",EDGE,{"derivedFrom":sQuery(id+"F0.wireOp",EDGE,"E8.5.0.0")}),-1.0]])]});
            var Q77;
            Q77=makeQuery(id+"F0.imprint","IMPRINT",FACE,{"disambiguationData":[TD([[makeQuery(id+"F0.imprint","IMPRINT",EDGE,{"derivedFrom":sQuery(id+"F0.wireOp",EDGE,"E3.5.0.0")}),-1.0]])]});
            var Q78;
            Q78=makeQuery(id+"F0.imprint","IMPRINT",FACE,{"disambiguationData":[TD([[makeQuery(id+"F0.imprint","IMPRINT",EDGE,{"derivedFrom":sQuery(id+"F0.wireOp",EDGE,"E3.3.0.0")}),-1.0]])]});
            var Q79;
            Q79=makeQuery(id+"F0.imprint","IMPRINT",FACE,{"disambiguationData":[TD([[makeQuery(id+"F0.imprint","IMPRINT",EDGE,{"derivedFrom":sQuery(id+"F0.wireOp",EDGE,"E3.2.0.0")}),-1.0]])]});
            var Q80;
            Q80=makeQuery(id+"F0.imprint","IMPRINT",FACE,{"disambiguationData":[TD([[makeQuery(id+"F0.imprint","IMPRINT",EDGE,{"derivedFrom":sQuery(id+"F0.wireOp",EDGE,"E3.4.0.0")}),-1.0]])]});
            var Q81;
            Q81=makeQuery(id+"F0.imprint","IMPRINT",FACE,{"disambiguationData":[TD([[makeQuery(id+"F0.imprint","IMPRINT",EDGE,{"derivedFrom":sQuery(id+"F0.wireOp",EDGE,"E3.6.0.0")}),-1.0]])]});
            var Q82;
            Q82=makeQuery(id+"F0.imprint","IMPRINT",FACE,{"disambiguationData":[TD([[makeQuery(id+"F0.imprint","IMPRINT",EDGE,{"derivedFrom":sQuery(id+"F0.wireOp",EDGE,"E3.1.0.0")}),-1.0]])]});
            var Q83;
            Q83=makeQuery(id+"F0.imprint","IMPRINT",FACE,{"disambiguationData":[TD([[makeQuery(id+"F0.imprint","IMPRINT",EDGE,{"derivedFrom":sQuery(id+"F0.wireOp",EDGE,"E1")}),1.0]])]});
            var Q84;
            Q84=makeQuery(id+"F0.imprint","IMPRINT",FACE,{"disambiguationData":[TD([[makeQuery(id+"F0.imprint","IMPRINT",EDGE,{"derivedFrom":sQuery(id+"F0.wireOp",EDGE,"E8.6.0.0")}),-1.0]])]});
            var Q85;
            Q85=makeQuery(id+"F0.imprint","IMPRINT",FACE,{"disambiguationData":[TD([[makeQuery(id+"F0.imprint","IMPRINT",EDGE,{"derivedFrom":sQuery(id+"F0.wireOp",EDGE,"E4.1.0.7")}),-1.0]])]});
            var Q86;
            Q86=makeQuery(id+"F0.imprint","IMPRINT",FACE,{"disambiguationData":[TD([[makeQuery(id+"F0.imprint","IMPRINT",EDGE,{"derivedFrom":sQuery(id+"F0.wireOp",EDGE,"E4.1.0.9")}),1.0]])]});
            var Q87;
            Q87=makeQuery(id+"F0.imprint","IMPRINT",FACE,{"disambiguationData":[TD([[makeQuery(id+"F0.imprint","IMPRINT",EDGE,{"derivedFrom":sQuery(id+"F0.wireOp",EDGE,"E8.7.0.2")}),-1.0]])]});
            var Q88;
            Q88=makeQuery(id+"F0.imprint","IMPRINT",FACE,{"disambiguationData":[TD([[makeQuery(id+"F0.imprint","IMPRINT",EDGE,{"derivedFrom":sQuery(id+"F0.wireOp",EDGE,"E4.2.0.17")}),-1.0]])]});
            var Q89;
            Q89=makeQuery(id+"F0.imprint","IMPRINT",FACE,{"disambiguationData":[TD([[makeQuery(id+"F0.imprint","IMPRINT",EDGE,{"derivedFrom":sQuery(id+"F0.wireOp",EDGE,"E8.7.0.0")}),-1.0]])]});
            var Q90;
            Q90=makeQuery(id+"F0.imprint","IMPRINT",FACE,{"disambiguationData":[TD([[makeQuery(id+"F0.imprint","IMPRINT",EDGE,{"derivedFrom":sQuery(id+"F0.wireOp",EDGE,"E3.7.0.0")}),-1.0]])]});
            var Q91;
            Q91=makeQuery(id+"F0.imprint","IMPRINT",FACE,{"disambiguationData":[TD([[makeQuery(id+"F0.imprint","IMPRINT",EDGE,{"derivedFrom":sQuery(id+"F0.wireOp",EDGE,"E3.8.0.0")}),-1.0]])]});
            var Q92;
            Q92=makeQuery(id+"F0.imprint","IMPRINT",FACE,{"disambiguationData":[TD([[makeQuery(id+"F0.imprint","IMPRINT",EDGE,{"derivedFrom":sQuery(id+"F0.wireOp",EDGE,"E4.2.0.16")}),-1.0]])]});
            var Q93;
            Q93=makeQuery(id+"F0.imprint","IMPRINT",FACE,{"disambiguationData":[TD([[makeQuery(id+"F0.imprint","IMPRINT",EDGE,{"derivedFrom":sQuery(id+"F0.wireOp",EDGE,"E8.9.0.2")}),-1.0]])]});
            var Q94;
            Q94=makeQuery(id+"F0.imprint","IMPRINT",FACE,{"disambiguationData":[TD([[makeQuery(id+"F0.imprint","IMPRINT",EDGE,{"derivedFrom":sQuery(id+"F0.wireOp",EDGE,"E8.8.0.2")}),-1.0]])]});
            var Q95;
            Q95=makeQuery(id+"F0.imprint","IMPRINT",FACE,{"disambiguationData":[TD([[makeQuery(id+"F0.imprint","IMPRINT",EDGE,{"derivedFrom":sQuery(id+"F0.wireOp",EDGE,"E4.1.0.17")}),-1.0]])]});
            var Q96;
            Q96=makeQuery(id+"F0.imprint","IMPRINT",FACE,{"disambiguationData":[TD([[makeQuery(id+"F0.imprint","IMPRINT",EDGE,{"derivedFrom":sQuery(id+"F0.wireOp",EDGE,"E4.1.0.16")}),-1.0]])]});
            var Q97;
            Q97=makeQuery(id+"F0.imprint","IMPRINT",FACE,{"disambiguationData":[TD([[makeQuery(id+"F0.imprint","IMPRINT",EDGE,{"derivedFrom":sQuery(id+"F0.wireOp",EDGE,"E8.8.0.0")}),-1.0]])]});
            var Q98;
            Q98=makeQuery(id+"F0.imprint","IMPRINT",FACE,{"disambiguationData":[TD([[makeQuery(id+"F0.imprint","IMPRINT",EDGE,{"derivedFrom":sQuery(id+"F0.wireOp",EDGE,"E8.9.0.0")}),-1.0]])]});
            var Q99;
            Q99=makeQuery(id+"F0.imprint","IMPRINT",FACE,{"disambiguationData":[TD([[makeQuery(id+"F0.imprint","IMPRINT",EDGE,{"derivedFrom":sQuery(id+"F0.wireOp",EDGE,"E3.9.0.0")}),-1.0]])]});
            var Q100;
            Q100=makeQuery(id+"F0.imprint","IMPRINT",FACE,{"disambiguationData":[TD([[makeQuery(id+"F0.imprint","IMPRINT",EDGE,{"derivedFrom":sQuery(id+"F0.wireOp",EDGE,"E0.bottom")}),1.0]])]});
            extrude(context, id + "F1", {"entities" : qUnion([Q0, Q1, Q2, Q3, Q4, Q5, Q6, Q7, Q8, Q9, Q10, Q11, Q12, Q13, Q14, Q15, Q16, Q17, Q18, Q19, Q20, Q21, Q22, Q23, Q24, Q25, Q26, Q27, Q28, Q29, Q30, Q31, Q32, Q33, Q34, Q35, Q36, Q37, Q38, Q39, Q40, Q41, Q42, Q43, Q44, Q45, Q46, Q47, Q48, Q49, Q50, Q51, Q52, Q53, Q54, Q55, Q56, Q57, Q58, Q59, Q60, Q61, Q62, Q63, Q64, Q65, Q66, Q67, Q68, Q69, Q70, Q71, Q72, Q73, Q74, Q75, Q76, Q77, Q78, Q79, Q80, Q81, Q82, Q83, Q84, Q85, Q86, Q87, Q88, Q89, Q90, Q91, Q92, Q93, Q94, Q95, Q96, Q97, Q98, Q99, Q100]), "oppositeDirection" : true, "depth" : 5.08 * mm, "offsetDistance" : 25.4 * mm});
        }
        {
            var Q0;
            Q0=makeQuery(id+"F0.imprint","IMPRINT",FACE,{"disambiguationData":[TD([[makeQuery(id+"F0.imprint","IMPRINT",EDGE,{"derivedFrom":sQuery(id+"F0.wireOp",EDGE,"E0.bottom")}),1.0]])]});
            extrude(context, id + "F2", {"entities" : qUnion([Q0]), "operationType" : NewBodyOperationType.ADD, "depth" : 20.32 * mm, "offsetDistance" : 25.4 * mm});
        }
        {
            var Q0;
            {var subQ0=sQuery(id+"F0.wireOp",EDGE,"E12");var subQ1=sQuery(id+"F0.wireOp",EDGE,"E0.right");Q0=makeQuery(id+"F2.boolean.opBoolean","MERGE",EDGE,{"derivedFrom":[makeQuery(id+"F1.opExtrude","SWEPT_EDGE",EDGE,{"disambiguationData":[OSD([subQ1,subQ0])]}),makeQuery(id+"F2.opExtrude","SWEPT_EDGE",EDGE,{"disambiguationData":[OSD([subQ1,subQ0])]})]});}
            var Q1;
            {var subQ0=sQuery(id+"F0.wireOp",EDGE,"E13");var subQ1=sQuery(id+"F0.wireOp",EDGE,"E10");Q1=makeQuery(id+"F2.boolean.opBoolean","MERGE",EDGE,{"derivedFrom":[makeQuery(id+"F1.opExtrude","SWEPT_EDGE",EDGE,{"disambiguationData":[OSD([subQ1,subQ0])]}),makeQuery(id+"F2.opExtrude","SWEPT_EDGE",EDGE,{"disambiguationData":[OSD([subQ1,subQ0])]})]});}
            var Q2;
            {var subQ0=sQuery(id+"F0.wireOp",EDGE,"E10");var subQ1=sQuery(id+"F0.wireOp",EDGE,"E9");Q2=makeQuery(id+"F2.boolean.opBoolean","MERGE",EDGE,{"derivedFrom":[makeQuery(id+"F1.opExtrude","SWEPT_EDGE",EDGE,{"disambiguationData":[OSD([subQ1,subQ0])]}),makeQuery(id+"F2.opExtrude","SWEPT_EDGE",EDGE,{"disambiguationData":[OSD([subQ1,subQ0])]})]});}
            var Q3;
            {var subQ0=sQuery(id+"F0.wireOp",EDGE,"E0.right");var subQ1=sQuery(id+"F0.wireOp",EDGE,"E0.bottom");Q3=makeQuery(id+"F2.boolean.opBoolean","MERGE",EDGE,{"derivedFrom":[makeQuery(id+"F1.opExtrude","SWEPT_EDGE",EDGE,{"disambiguationData":[OSD([subQ1,subQ0])]}),makeQuery(id+"F2.opExtrude","SWEPT_EDGE",EDGE,{"disambiguationData":[OSD([subQ1,subQ0])]})]});}
            fillet(context, id + "F3", {"entities" : qUnion([Q0, Q1, Q2, Q3]), "radius" : 7.97 * mm, "tangentPropagation" : true, "allowEdgeOverflow" : false});
        }
        {
            var Q0;
            Q0=makeQuery(id+"F1.opExtrude","CAP_EDGE",EDGE,{"disambiguationData":[OSD([sQuery(id+"F0.wireOp",EDGE,"E0.right")])],"isStart":false});
            chamfer(context, id + "F4", {"entities" : qUnion([Q0]), "width" : 1.78 * mm, "tangentPropagation" : true});
        }
        {
            var Q0;
            Q0=makeQuery(id+"F2.opExtrude","CAP_FACE",FACE,{"disambiguationData":[OSD([sQuery(id+"F0.wireOp",EDGE,"E0.bottom"),sQuery(id+"F0.wireOp",EDGE,"E0.right"),sQuery(id+"F0.wireOp",EDGE,"E1"),sQuery(id+"F0.wireOp",EDGE,"E3.1.0.1"),sQuery(id+"F0.wireOp",EDGE,"E3.2.0.1"),sQuery(id+"F0.wireOp",EDGE,"E3.3.0.1"),sQuery(id+"F0.wireOp",EDGE,"E3.4.0.1"),sQuery(id+"F0.wireOp",EDGE,"E3.5.0.1"),sQuery(id+"F0.wireOp",EDGE,"E3.6.0.1"),sQuery(id+"F0.wireOp",EDGE,"E3.7.0.1"),sQuery(id+"F0.wireOp",EDGE,"E3.8.0.1"),sQuery(id+"F0.wireOp",EDGE,"E3.9.0.1"),sQuery(id+"F0.wireOp",EDGE,"E4.1.0.1"),sQuery(id+"F0.wireOp",EDGE,"E4.1.0.5"),sQuery(id+"F0.wireOp",EDGE,"E4.1.0.6"),sQuery(id+"F0.wireOp",EDGE,"E4.1.0.8"),sQuery(id+"F0.wireOp",EDGE,"E4.1.0.9"),sQuery(id+"F0.wireOp",EDGE,"E4.1.0.10"),sQuery(id+"F0.wireOp",EDGE,"E4.1.0.12"),sQuery(id+"F0.wireOp",EDGE,"E4.1.0.13"),sQuery(id+"F0.wireOp",EDGE,"E4.1.0.18"),sQuery(id+"F0.wireOp",EDGE,"E4.1.0.19"),sQuery(id+"F0.wireOp",EDGE,"E4.2.0.1"),sQuery(id+"F0.wireOp",EDGE,"E4.2.0.5"),sQuery(id+"F0.wireOp",EDGE,"E4.2.0.6"),sQuery(id+"F0.wireOp",EDGE,"E4.2.0.8"),sQuery(id+"F0.wireOp",EDGE,"E4.2.0.9"),sQuery(id+"F0.wireOp",EDGE,"E4.2.0.10"),sQuery(id+"F0.wireOp",EDGE,"E4.2.0.12"),sQuery(id+"F0.wireOp",EDGE,"E4.2.0.13"),sQuery(id+"F0.wireOp",EDGE,"E4.2.0.18"),sQuery(id+"F0.wireOp",EDGE,"E4.2.0.19"),sQuery(id+"F0.wireOp",EDGE,"E4.3.0.1"),sQuery(id+"F0.wireOp",EDGE,"E4.3.0.5"),sQuery(id+"F0.wireOp",EDGE,"E4.3.0.6"),sQuery(id+"F0.wireOp",EDGE,"E4.3.0.8"),sQuery(id+"F0.wireOp",EDGE,"E4.3.0.9"),sQuery(id+"F0.wireOp",EDGE,"E4.3.0.10"),sQuery(id+"F0.wireOp",EDGE,"E4.3.0.12"),sQuery(id+"F0.wireOp",EDGE,"E4.3.0.13"),sQuery(id+"F0.wireOp",EDGE,"E4.3.0.18"),sQuery(id+"F0.wireOp",EDGE,"E4.3.0.19"),sQuery(id+"F0.wireOp",EDGE,"E4.4.0.1"),sQuery(id+"F0.wireOp",EDGE,"E4.4.0.5"),sQuery(id+"F0.wireOp",EDGE,"E4.4.0.6"),sQuery(id+"F0.wireOp",EDGE,"E4.4.0.8"),sQuery(id+"F0.wireOp",EDGE,"E4.4.0.9"),sQuery(id+"F0.wireOp",EDGE,"E4.4.0.10"),sQuery(id+"F0.wireOp",EDGE,"E4.4.0.12"),sQuery(id+"F0.wireOp",EDGE,"E4.4.0.13"),sQuery(id+"F0.wireOp",EDGE,"E4.4.0.18"),sQuery(id+"F0.wireOp",EDGE,"E4.4.0.19"),sQuery(id+"F0.wireOp",EDGE,"E5"),sQuery(id+"F0.wireOp",EDGE,"E7.1.0.1"),sQuery(id+"F0.wireOp",EDGE,"E7.2.0.1"),sQuery(id+"F0.wireOp",EDGE,"E7.3.0.1"),sQuery(id+"F0.wireOp",EDGE,"E7.4.0.1"),sQuery(id+"F0.wireOp",EDGE,"E8.1.0.1"),sQuery(id+"F0.wireOp",EDGE,"E8.1.0.3"),sQuery(id+"F0.wireOp",EDGE,"E8.1.0.5"),sQuery(id+"F0.wireOp",EDGE,"E8.1.0.7"),sQuery(id+"F0.wireOp",EDGE,"E8.1.0.9"),sQuery(id+"F0.wireOp",EDGE,"E8.2.0.1"),sQuery(id+"F0.wireOp",EDGE,"E8.2.0.3"),sQuery(id+"F0.wireOp",EDGE,"E8.2.0.5"),sQuery(id+"F0.wireOp",EDGE,"E8.2.0.7"),sQuery(id+"F0.wireOp",EDGE,"E8.2.0.9"),sQuery(id+"F0.wireOp",EDGE,"E8.3.0.1"),sQuery(id+"F0.wireOp",EDGE,"E8.3.0.3"),sQuery(id+"F0.wireOp",EDGE,"E8.3.0.5"),sQuery(id+"F0.wireOp",EDGE,"E8.3.0.7"),sQuery(id+"F0.wireOp",EDGE,"E8.3.0.9"),sQuery(id+"F0.wireOp",EDGE,"E8.4.0.1"),sQuery(id+"F0.wireOp",EDGE,"E8.4.0.3"),sQuery(id+"F0.wireOp",EDGE,"E8.4.0.5"),sQuery(id+"F0.wireOp",EDGE,"E8.4.0.7"),sQuery(id+"F0.wireOp",EDGE,"E8.4.0.9"),sQuery(id+"F0.wireOp",EDGE,"E8.5.0.1"),sQuery(id+"F0.wireOp",EDGE,"E8.5.0.3"),sQuery(id+"F0.wireOp",EDGE,"E8.5.0.5"),sQuery(id+"F0.wireOp",EDGE,"E8.5.0.7"),sQuery(id+"F0.wireOp",EDGE,"E8.5.0.9"),sQuery(id+"F0.wireOp",EDGE,"E8.6.0.1"),sQuery(id+"F0.wireOp",EDGE,"E8.6.0.3"),sQuery(id+"F0.wireOp",EDGE,"E8.6.0.5"),sQuery(id+"F0.wireOp",EDGE,"E8.6.0.7"),sQuery(id+"F0.wireOp",EDGE,"E8.6.0.9"),sQuery(id+"F0.wireOp",EDGE,"E8.7.0.1"),sQuery(id+"F0.wireOp",EDGE,"E8.7.0.3"),sQuery(id+"F0.wireOp",EDGE,"E8.7.0.5"),sQuery(id+"F0.wireOp",EDGE,"E8.7.0.7"),sQuery(id+"F0.wireOp",EDGE,"E8.7.0.9"),sQuery(id+"F0.wireOp",EDGE,"E8.8.0.1"),sQuery(id+"F0.wireOp",EDGE,"E8.8.0.3"),sQuery(id+"F0.wireOp",EDGE,"E8.8.0.5"),sQuery(id+"F0.wireOp",EDGE,"E8.8.0.7"),sQuery(id+"F0.wireOp",EDGE,"E8.8.0.9"),sQuery(id+"F0.wireOp",EDGE,"E8.9.0.1"),sQuery(id+"F0.wireOp",EDGE,"E8.9.0.3"),sQuery(id+"F0.wireOp",EDGE,"E8.9.0.5"),sQuery(id+"F0.wireOp",EDGE,"E8.9.0.7"),sQuery(id+"F0.wireOp",EDGE,"E8.9.0.9"),sQuery(id+"F0.wireOp",EDGE,"E9"),sQuery(id+"F0.wireOp",EDGE,"E10"),sQuery(id+"F0.wireOp",EDGE,"E11"),sQuery(id+"F0.wireOp",EDGE,"E12"),sQuery(id+"F0.wireOp",EDGE,"E13")])],"isStart":false});
            cPlane(context, id + "F5", {"entities" : qUnion([Q0]), "cplaneType" : CPlaneType.OFFSET, "offset" : 25.4 * mm, "width" : 152.4 * mm, "height" : 152.4 * mm});
        }
        {
            var Q0;
            Q0=qCreatedBy(id+"F5.planeOp",FACE);
            var sketch = newSketch(context, id + "F6", { "sketchPlane" : qUnion([Q0])});
            skText(sketch, "E16", { "text": "K", "fontName": "OpenSans-Regular.ttf"});
            skText(sketch, "E17", { "text": "E", "fontName": "OpenSans-Regular.ttf"});
            skText(sketch, "E18", { "text": "N", "fontName": "OpenSans-Regular.ttf"});
            skText(sketch, "E19", { "text": "T", "fontName": "OpenSans-Regular.ttf"});
            const initialGuessF6  = {"E16": [-0.07601, 0.0521, 1, 0, 0.01008], "E17": [-0.0759, 0.02969, 1, 0, 0.00968], "E18": [-0.07704, 0.00636, 1, 0, 0.01046], "E19": [-0.07559, -0.01643, 1, 0, 0.0105]};
            skSetInitialGuess(sketch, initialGuessF6);
            skSolve(sketch);
        }
        {
            var Q0;
            Q0 = qSketchRegion(id + "F6", true);
            extrude(context, id + "F7", {"entities" : qUnion([Q0]), "operationType" : NewBodyOperationType.REMOVE, "oppositeDirection" : true, "depth" : 26.44 * mm, "offsetDistance" : 25.4 * mm});
        }
    });
